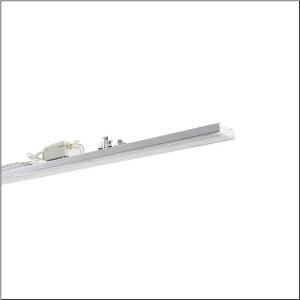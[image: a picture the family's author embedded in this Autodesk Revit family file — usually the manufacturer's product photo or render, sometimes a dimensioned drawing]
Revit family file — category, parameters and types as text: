
# Revit family: licross_r__21_recessed_ho_52tl12mn4fxm_f100
name_source: partatom
category: Lighting Fixtures
units: mm (PartAtom-declared; Revit-internal decimal feet)

## family parameters
Cut with Voids When Loaded = No
Host = Face
Light Source = No
Part Type = Normal
Room Calculation Point = No
Round Connector Dimension = Use Diameter
Shared = No

## types (1)
- --- (1 x LED, 15100 lm, 83.1 W, 4000K)
    Apparent Load = 83 VA
    CIE Flux Codes = 69 91 98 100 100
    Color Rendering = 80
    Color Temperature = 4000K
    Default Elevation = 1800 mm
    Description = Licross® 21 Recessed HO, luminaire insert, of sheet steel, galvanised, coil coated, white, length: 1.500mm, width: 66mm, height: 67mm, LED rated luminous flux: 15.100lm, light colour: 840, control gear: ON/OFF Multilumen, with plug, 3-pole, with phase selection, mains connection: 220..240V, AC, 50/60Hz, rated input power: 83W, halogen-free wiring, primary optical cover: cover, of PMMA, light emission: direct distribution, primary light characteristic: symmetric, protection rating (complete): IP40, insulation class (complete): insulation class I (protective earthing), certification: CE, ENEC, VDE, UKCA, protection symbol: D if used in an environment without relevant dust loads with corresponding accessories, impact resistance: IK06, permissible ambient temperature for indoor applications: -35..+30°C, corresponds to IFS (International Featured Standards) requirements for safety and quality in the food industry, reducing of maximum allowable ambient temperature of 5°C with ceiling mounting, LABS conformity tested according to VDMA 24364:2018-05, packaging unit: 1 piece
    Height = 58 mm
    Lamp = 1 x LED
    Lamp Light Flux = 15100 lm
    Lamp Power = 83.1 W
    Lamp count = 1
    Length = 1500 mm
    Luminous efficacy = 182 lm/W
    Manufacturer = Siteco
    ModVariant = No
    Model = 52TL12MN4FXM
    Mounting Place = Ceiling
    Mounting Type = Pendant
    Number of Poles = 1
    OnlyDefault = Yes
    Power Factor = 1
    Product Name = Licross® 21 Recessed HO
    Product group = luminaire insert
    ProductGroupID = 901
    Protection Class = Protection class I
    Protection Degree = IP 40
    RLX_Detail_Level = 1
    RLX_Emergency_Light_Flux = 0 lm
    RLX_Emergency_Type = 0
    RLX_Emergency_Type_DB = No
    RlxData = <blob elided: 22337 chars, md5=1a697848>
    Socket = socket
    Standby Power = 0 W
    System Light Flux = 15100 lm
    System Power = 83 W
    Type Comments = factory setting: luminous flux: 100 % | (A | C | E) | 195 mA
    Type Image = l_1296930.jpg
    URL = http://relux.com
    VarID = @adj_033295
    Voltage = 0 V
    Weight = 0.00 kg
    Width = 66 mm

## geometry (parser evidence)
native form markers: Blend x4, Sweep x12
no freeform markers — native parametric forms only
